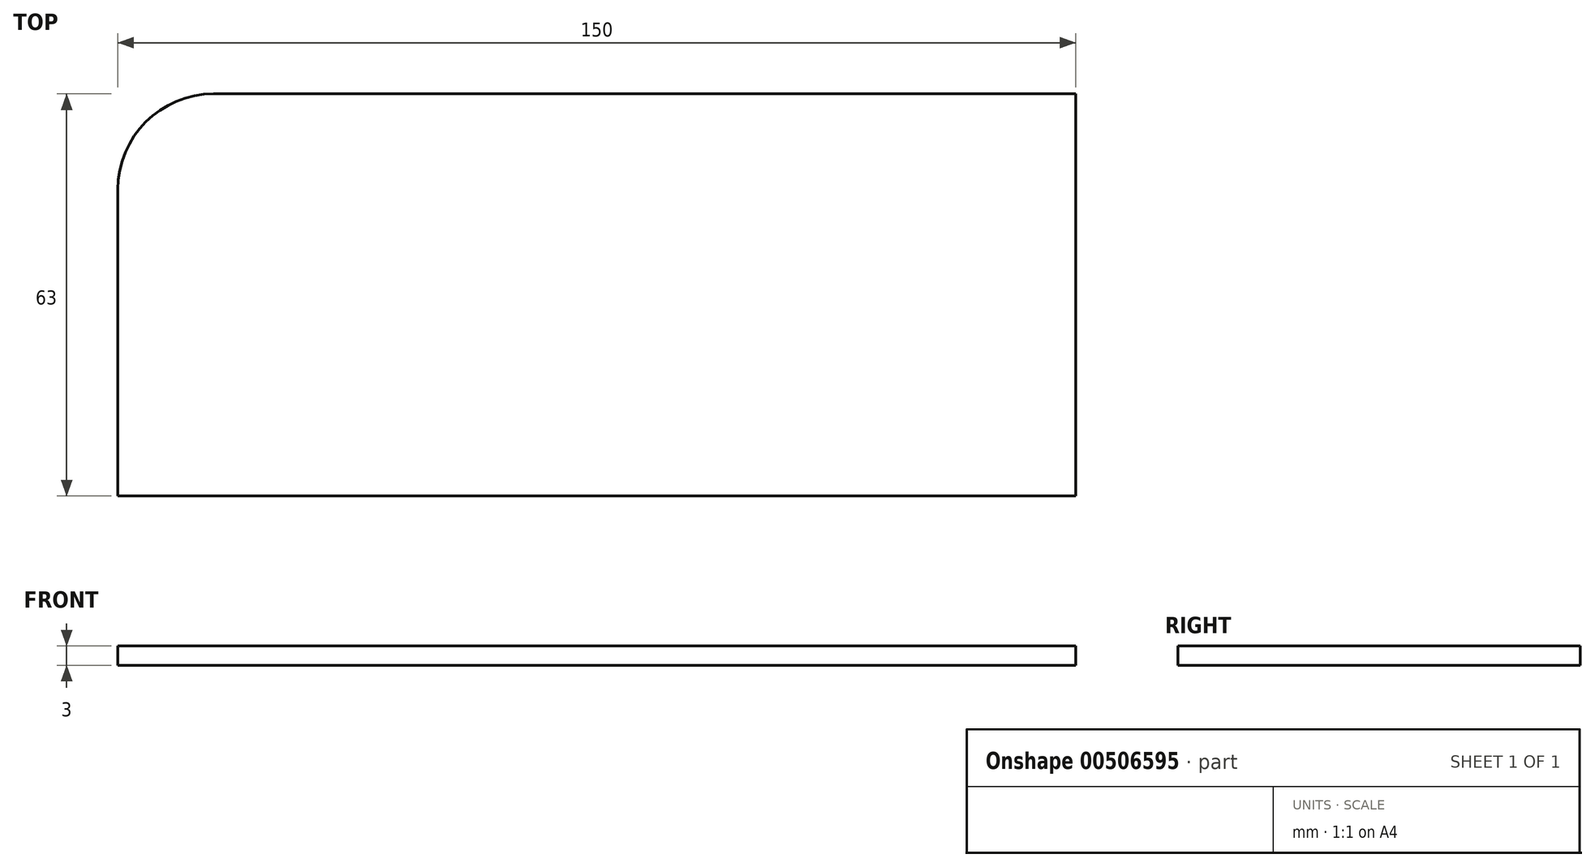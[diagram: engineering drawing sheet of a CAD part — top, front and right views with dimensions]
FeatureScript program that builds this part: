
annotation { "Feature Type Name" : "Feature", "Feature Type Description" : "" }
export const myFeature = defineFeature(function(context is Context, id is Id, definition is map)
    precondition{}
    {
        {
            var Q0;
            Q0=qCreatedBy(makeId("Top.planeOp"),FACE);
            var sketch = newSketch(context, id + "F0", { "sketchPlane" : qUnion([Q0])});
            skLineSegment(sketch, "E0.bottom", {"start": v(-33.27, 39.37) * mm, "end": v(101.73, 39.37) * mm});
            skLineSegment(sketch, "E0.top", {"start": v(-48.27, -23.63) * mm, "end": v(101.73, -23.63) * mm});
            skLineSegment(sketch, "E0.left", {"start": v(-48.27, 24.37) * mm, "end": v(-48.27, -23.63) * mm});
            skLineSegment(sketch, "E0.right", {"start": v(101.73, 39.37) * mm, "end": v(101.73, -23.63) * mm});
            skPoint(sketch, "E1.visualSharp", {"position": v(-48.27, 39.37) * mm});
            skArc(sketch, "E1.filletArc", {"start": v(-33.27, 39.37) * mm, "mid": v(-43.88, 34.97) * mm, "end": v(-48.27, 24.37) * mm});
            skSolve(sketch);
        }
        {
            var Q0;
            Q0 = qSketchRegion(id + "F0", true);
            extrude(context, id + "F1", {"entities" : qUnion([Q0]), "depth" : 3 * mm});
        }
    });
